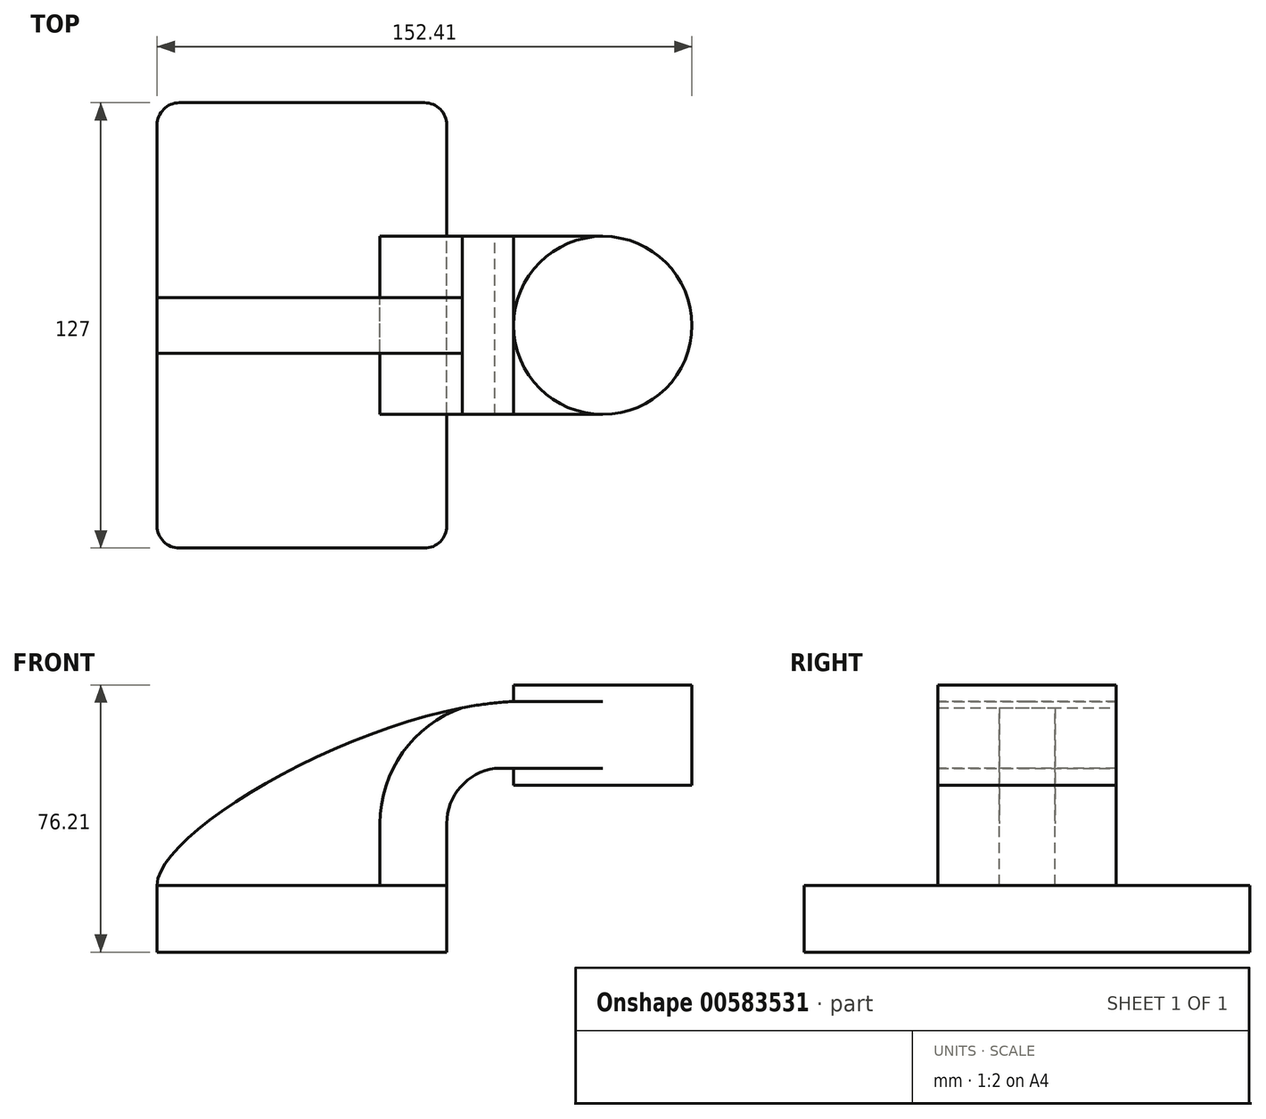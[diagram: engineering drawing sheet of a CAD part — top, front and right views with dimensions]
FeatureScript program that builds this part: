
annotation { "Feature Type Name" : "Feature", "Feature Type Description" : "" }
export const myFeature = defineFeature(function(context is Context, id is Id, definition is map)
    precondition{}
    {
        {
            var Q0;
            Q0=qCreatedBy(makeId("Front.planeOp"),FACE);
            var sketch = newSketch(context, id + "F0", { "sketchPlane" : qUnion([Q0])});
            skLineSegment(sketch, "E0.bottom", {"start": v(41.28, -9.52) * mm, "end": v(-41.28, -9.53) * mm});
            skLineSegment(sketch, "E0.top", {"start": v(41.28, 9.53) * mm, "end": v(-41.28, 9.52) * mm});
            skLineSegment(sketch, "E0.left", {"start": v(41.28, -9.52) * mm, "end": v(41.28, 9.53) * mm});
            skLineSegment(sketch, "E0.right", {"start": v(-41.28, -9.53) * mm, "end": v(-41.28, 9.52) * mm});
            skPoint(sketch, "E0.middle", {"position": v(0, 0) * mm});
            skLineSegment(sketch, "E1.bottom", {"start": v(111.12, 38.1) * mm, "end": v(60.32, 38.1) * mm});
            skLineSegment(sketch, "E1.top", {"start": v(111.12, 66.68) * mm, "end": v(60.32, 66.68) * mm});
            skLineSegment(sketch, "E1.left", {"start": v(111.12, 38.1) * mm, "end": v(111.12, 66.68) * mm});
            skLineSegment(sketch, "E1.right", {"start": v(60.32, 38.1) * mm, "end": v(60.32, 66.68) * mm});
            skPoint(sketch, "E1.middle", {"position": v(85.72, 52.39) * mm});
            skLineSegment(sketch, "E2", {"start": v(41.28, 9.53) * mm, "end": v(41.28, 27.14) * mm});
            skArc(sketch, "E3", {"start": v(41.28, 27.14) * mm, "mid": v(45.2, 37.59) * mm, "end": v(55.01, 42.88) * mm});
            skLineSegment(sketch, "E4", {"start": v(55.01, 42.88) * mm, "end": v(85.72, 42.88) * mm});
            skPoint(sketch, "E4.endSnap0", {"position": v(85.72, 38.1) * mm});
            skLineSegment(sketch, "E5.0", {"start": v(60.32, 61.93) * mm, "end": v(85.72, 61.93) * mm});
            skArc(sketch, "E5.1", {"start": v(22.23, 27.14) * mm, "mid": v(33.6, 52.94) * mm, "end": v(60.32, 61.93) * mm});
            skLineSegment(sketch, "E5.2", {"start": v(22.23, 9.53) * mm, "end": v(22.23, 27.14) * mm});
            skLineSegment(sketch, "E6", {"start": v(85.72, 38.1) * mm, "end": v(85.72, 66.68) * mm});
            skFitSpline(sketch, "E7", {"points": [v(-41.28, 9.52) * mm, v(60.32, 61.93) * mm], "startDerivative": vector(0.04, 47.72) * mm, "endDerivative": vector(122.74, 5.02) * mm});
            skSolve(sketch);
        }
        {
            var Q0;
            Q0=makeQuery(id+"F0.imprint","IMPRINT",FACE,{"disambiguationData":[TD([[makeQuery(id+"F0.imprint","IMPRINT",EDGE,{"derivedFrom":sQuery(id+"F0.wireOp",EDGE,"E0.bottom")}),-1.0]])]});
            extrude(context, id + "F1", {"entities" : qUnion([Q0]), "endBound" : BoundingType.SYMMETRIC, "depth" : 127 * mm, "offsetDistance" : 25.4 * mm});
        }
        {
            var Q0;
            {var subQ6=sQuery(id+"F0.wireOp",EDGE,"E2");Q0=makeQuery(id+"F0.imprint","IMPRINT",FACE,{"disambiguationData":[TD([[makeQuery(id+"F0.imprint","IMPRINT",EDGE,{"derivedFrom":subQ6}),1.0]])]});}
            var Q1;
            {var subQ0=sQuery(id+"F0.wireOp",EDGE,"E5.0");Q1=makeQuery(id+"F0.imprint","IMPRINT",FACE,{"disambiguationData":[TD([[makeQuery(id+"F0.imprint","IMPRINT",EDGE,{"derivedFrom":subQ0}),-1.0]])]});}
            extrude(context, id + "F2", {"entities" : qUnion([Q0, Q1]), "endBound" : BoundingType.SYMMETRIC, "depth" : 50.8 * mm, "offsetDistance" : 25.4 * mm});
        }
        {
            var Q0;
            {var subQ3=sQuery(id+"F0.wireOp",EDGE,"E5.2");Q0=makeQuery(id+"F0.imprint","IMPRINT",FACE,{"disambiguationData":[TD([[makeQuery(id+"F0.imprint","IMPRINT",EDGE,{"derivedFrom":subQ3}),1.0]])]});}
            extrude(context, id + "F3", {"entities" : qUnion([Q0]), "endBound" : BoundingType.SYMMETRIC, "depth" : 15.88 * mm, "offsetDistance" : 25.4 * mm});
        }
        {
            var Q0;
            {var subQ4=sQuery(id+"F0.wireOp",EDGE,"E1.left");Q0=makeQuery(id+"F0.imprint","IMPRINT",FACE,{"disambiguationData":[TD([[makeQuery(id+"F0.imprint","IMPRINT",EDGE,{"derivedFrom":subQ4}),1.0]])]});}
            var Q1;
            Q1=sQuery(id+"F0.wireOp",EDGE,"E6");
            revolve(context, id + "F4", {"operationType" : NewBodyOperationType.ADD, "entities" : qUnion([Q0]), "axis" : qUnion([Q1]), "revolveType" : RevolveType.FULL});
        }
        {
            var Q0;
            Q0=makeQuery(id+"F1.opExtrude","CAP_EDGE",EDGE,{"disambiguationData":[OSD([sQuery(id+"F0.wireOp",EDGE,"E0.left")])],"isStart":false});
            var Q1;
            Q1=makeQuery(id+"F1.opExtrude","CAP_EDGE",EDGE,{"disambiguationData":[OSD([sQuery(id+"F0.wireOp",EDGE,"E0.right")])],"isStart":false});
            var Q2;
            Q2=makeQuery(id+"F1.opExtrude","CAP_EDGE",EDGE,{"disambiguationData":[OSD([sQuery(id+"F0.wireOp",EDGE,"E0.left")])],"isStart":true});
            var Q3;
            Q3=makeQuery(id+"F1.opExtrude","CAP_EDGE",EDGE,{"disambiguationData":[OSD([sQuery(id+"F0.wireOp",EDGE,"E0.right")])],"isStart":true});
            fillet(context, id + "F5", {"entities" : qUnion([Q0, Q1, Q2, Q3]), "radius" : 6.35 * mm, "tangentPropagation" : true, "allowEdgeOverflow" : false});
        }
    });
